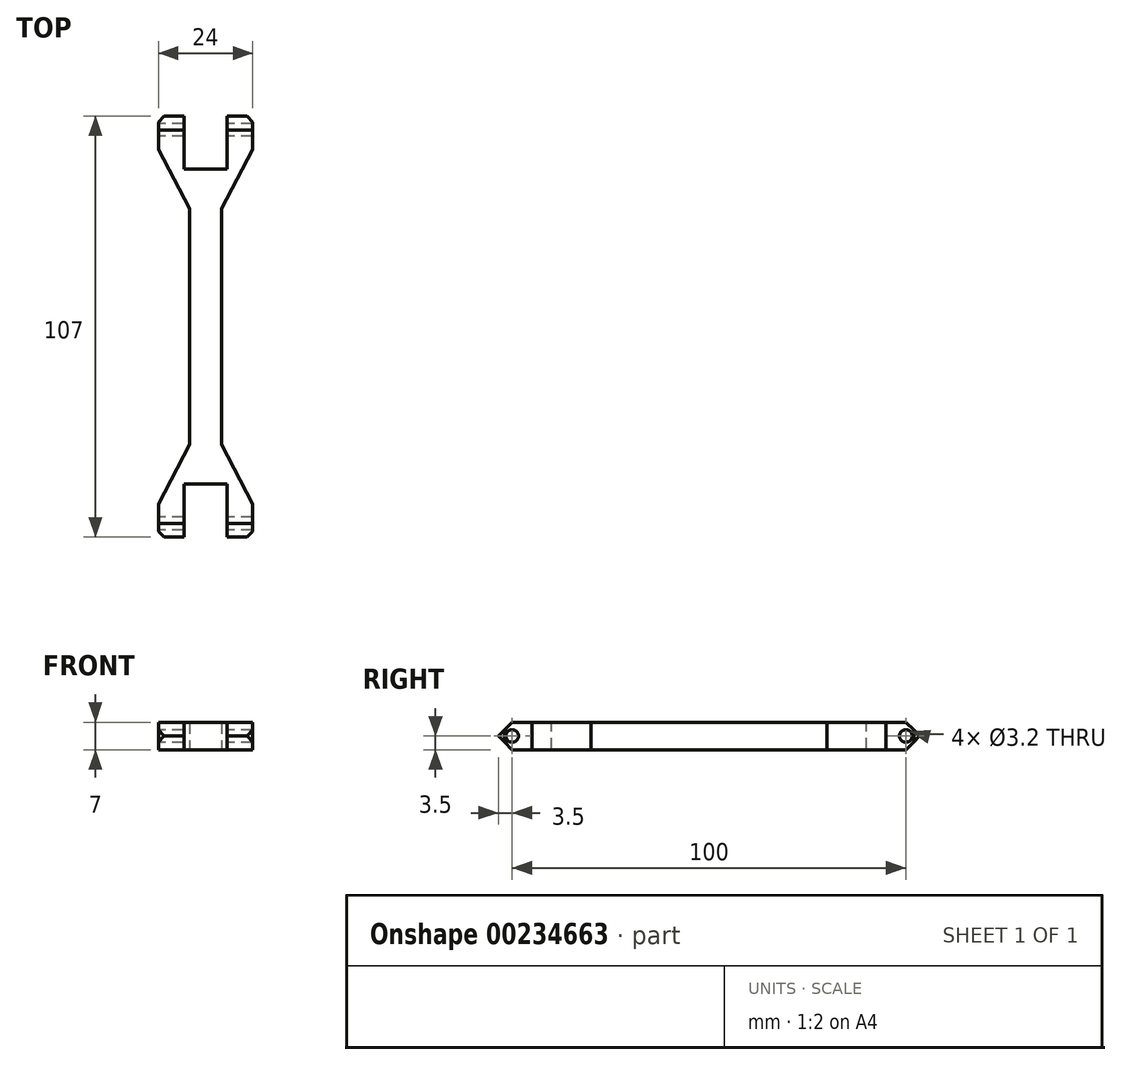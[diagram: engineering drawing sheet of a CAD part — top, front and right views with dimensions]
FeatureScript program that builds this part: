
annotation { "Feature Type Name" : "Feature", "Feature Type Description" : "" }
export const myFeature = defineFeature(function(context is Context, id is Id, definition is map)
    precondition{}
    {
        {
            var Q0;
            Q0=qCreatedBy(makeId("Top.planeOp"),FACE);
            var sketch = newSketch(context, id + "F0", { "sketchPlane" : qUnion([Q0])});
            skLineSegment(sketch, "E0.bottom", {"start": v(-4, 45) * mm, "end": v(4, 45) * mm});
            skLineSegment(sketch, "E0.top", {"start": v(-4, -45) * mm, "end": v(4, -45) * mm});
            skLineSegment(sketch, "E0.left", {"start": v(-4, 45) * mm, "end": v(-4, -45) * mm});
            skLineSegment(sketch, "E0.right", {"start": v(4, 45) * mm, "end": v(4, -45) * mm});
            skPoint(sketch, "E0.middle", {"position": v(0, 0) * mm});
            skLineSegment(sketch, "E1", {"start": v(-4, 45) * mm, "end": v(-12, 45) * mm});
            skLineSegment(sketch, "E2", {"start": v(4, 45) * mm, "end": v(12, 45) * mm});
            skLineSegment(sketch, "E3", {"start": v(12, 45) * mm, "end": v(12, 55) * mm});
            skLineSegment(sketch, "E4", {"start": v(-12, 45) * mm, "end": v(-12, 55) * mm});
            skLineSegment(sketch, "E5", {"start": v(-12, 55) * mm, "end": v(-5.5, 55) * mm});
            skLineSegment(sketch, "E6", {"start": v(12, 55) * mm, "end": v(5.5, 55) * mm});
            skLineSegment(sketch, "E7", {"start": v(-5.5, 55) * mm, "end": v(-5.5, 45) * mm});
            skLineSegment(sketch, "E8", {"start": v(-5.5, 45) * mm, "end": v(5.5, 45) * mm});
            skLineSegment(sketch, "E9", {"start": v(5.5, 45) * mm, "end": v(5.5, 55) * mm});
            skLineSegment(sketch, "E10", {"start": v(4, -45) * mm, "end": v(12, -45) * mm});
            skLineSegment(sketch, "E11", {"start": v(-4, -45) * mm, "end": v(-12, -45) * mm});
            skLineSegment(sketch, "E12", {"start": v(-12, -45) * mm, "end": v(-12, -55) * mm});
            skLineSegment(sketch, "E13", {"start": v(12, -45) * mm, "end": v(12, -55) * mm});
            skLineSegment(sketch, "E14", {"start": v(12, -55) * mm, "end": v(5.5, -55) * mm});
            skLineSegment(sketch, "E15", {"start": v(-12, -55) * mm, "end": v(-5.5, -55) * mm});
            skLineSegment(sketch, "E16", {"start": v(-5.5, -55) * mm, "end": v(-5.5, -45) * mm});
            skLineSegment(sketch, "E17", {"start": v(-5.5, -45) * mm, "end": v(5.5, -45) * mm});
            skLineSegment(sketch, "E18", {"start": v(5.5, -45) * mm, "end": v(5.5, -55) * mm});
            skLineSegment(sketch, "E19", {"start": v(0, -45) * mm, "end": v(0, 0) * mm});
            skLineSegment(sketch, "E20", {"start": v(0, 45) * mm, "end": v(0, 0) * mm});
            skLineSegment(sketch, "E21", {"start": v(-12, 45) * mm, "end": v(0, 22.5) * mm});
            skLineSegment(sketch, "E22", {"start": v(0, 22.5) * mm, "end": v(12, 45) * mm});
            skLineSegment(sketch, "E23", {"start": v(12, -45) * mm, "end": v(0, -22.5) * mm});
            skLineSegment(sketch, "E24", {"start": v(0, -22.5) * mm, "end": v(-12, -45) * mm});
            skSolve(sketch);
        }
        {
            var Q0;
            {var subQ3=sQuery(id+"F0.wireOp",EDGE,"E0.bottom");Q0=makeQuery(id+"F0.imprint","IMPRINT",FACE,{"disambiguationData":[TD([[makeQuery(id+"F0.imprint","IMPRINT",EDGE,{"derivedFrom":subQ3}),-1.0]])]});}
            var Q1;
            {var subQ0=sQuery(id+"F0.wireOp",EDGE,"E1");Q1=makeQuery(id+"F0.imprint","IMPRINT",FACE,{"disambiguationData":[TD([[makeQuery(id+"F0.imprint","IMPRINT",EDGE,{"derivedFrom":subQ0}),1.0]])]});}
            var Q2;
            Q2=makeQuery(id+"F0.imprint","IMPRINT",FACE,{"disambiguationData":[TD([[makeQuery(id+"F0.imprint","IMPRINT",EDGE,{"derivedFrom":sQuery(id+"F0.wireOp",EDGE,"E0.bottom")}),1.0]])]});
            var Q3;
            Q3=makeQuery(id+"F0.imprint","IMPRINT",FACE,{"disambiguationData":[TD([[makeQuery(id+"F0.imprint","IMPRINT",EDGE,{"derivedFrom":sQuery(id+"F0.wireOp",EDGE,"E0.top")}),-1.0]])]});
            var Q4;
            {var subQ0=sQuery(id+"F0.wireOp",EDGE,"E10");Q4=makeQuery(id+"F0.imprint","IMPRINT",FACE,{"disambiguationData":[TD([[makeQuery(id+"F0.imprint","IMPRINT",EDGE,{"derivedFrom":subQ0}),1.0]])]});}
            var Q5;
            {var subQ3=sQuery(id+"F0.wireOp",EDGE,"cfKpiMNQ-YmFG-QDXa-ybqN-YLsFEOFvvFe6");Q5=makeQuery(id+"F0.imprint","IMPRINT",FACE,{"disambiguationData":[TD([[makeQuery(id+"F0.imprint","IMPRINT",EDGE,{"derivedFrom":subQ3}),1.0]])]});}
            var Q6;
            {var subQ0=sQuery(id+"F0.wireOp",EDGE,"E11");Q6=makeQuery(id+"F0.imprint","IMPRINT",FACE,{"disambiguationData":[TD([[makeQuery(id+"F0.imprint","IMPRINT",EDGE,{"derivedFrom":subQ0}),-1.0]])]});}
            var Q7;
            {var subQ0=sQuery(id+"F0.wireOp",EDGE,"E2");Q7=makeQuery(id+"F0.imprint","IMPRINT",FACE,{"disambiguationData":[TD([[makeQuery(id+"F0.imprint","IMPRINT",EDGE,{"derivedFrom":subQ0}),-1.0]])]});}
            var Q8;
            {var subQ3=sQuery(id+"F0.wireOp",EDGE,"P5ZGW9Wr-uCcD-RAwQ-2Qk7-HA82AO7tK8vU");Q8=makeQuery(id+"F0.imprint","IMPRINT",FACE,{"disambiguationData":[TD([[makeQuery(id+"F0.imprint","IMPRINT",EDGE,{"derivedFrom":subQ3}),-1.0]])]});}
            var Q9;
            {var subQ0=sQuery(id+"F0.wireOp",EDGE,"E21");var subQ3=sQuery(id+"F0.wireOp",EDGE,"E0.left");var subQ4=makeQuery(id+"F0.imprint","INTERSECT",VERTEX,{"derivedFrom":[subQ3,subQ0]});Q9=makeQuery(id+"F0.imprint","IMPRINT",FACE,{"disambiguationData":[TD([[makeQuery(id+"F0.imprint","IMPRINT",EDGE,{"disambiguationData":[TD([[subQ4,-1.0]])],"derivedFrom":subQ3}),1.0]])]});}
            var Q10;
            {var subQ1=sQuery(id+"F0.wireOp",EDGE,"E0.top");var subQ3=sQuery(id+"F0.wireOp",EDGE,"E19");var subQ4=makeQuery(id+"F0.imprint","INTERSECT",VERTEX,{"derivedFrom":[subQ1,subQ3]});Q10=makeQuery(id+"F0.imprint","IMPRINT",FACE,{"disambiguationData":[TD([[makeQuery(id+"F0.imprint","IMPRINT",EDGE,{"disambiguationData":[TD([[subQ4,-1.0]])],"derivedFrom":subQ1}),1.0]])]});}
            var Q11;
            {var subQ1=sQuery(id+"F0.wireOp",EDGE,"E0.top");var subQ3=sQuery(id+"F0.wireOp",EDGE,"E19");var subQ4=makeQuery(id+"F0.imprint","INTERSECT",VERTEX,{"derivedFrom":[subQ1,subQ3]});Q11=makeQuery(id+"F0.imprint","IMPRINT",FACE,{"disambiguationData":[TD([[makeQuery(id+"F0.imprint","IMPRINT",EDGE,{"disambiguationData":[TD([[subQ4,1.0]])],"derivedFrom":subQ1}),1.0]])]});}
            var Q12;
            {var subQ0=sQuery(id+"F0.wireOp",EDGE,"E22");var subQ3=sQuery(id+"F0.wireOp",EDGE,"E0.right");var subQ4=makeQuery(id+"F0.imprint","INTERSECT",VERTEX,{"derivedFrom":[subQ3,subQ0]});Q12=makeQuery(id+"F0.imprint","IMPRINT",FACE,{"disambiguationData":[TD([[makeQuery(id+"F0.imprint","IMPRINT",EDGE,{"disambiguationData":[TD([[subQ4,-1.0]])],"derivedFrom":subQ3}),-1.0]])]});}
            var Q13;
            {var subQ0=sQuery(id+"F0.wireOp",EDGE,"E8");var subQ1=sQuery(id+"F0.wireOp",EDGE,"E0.left");var subQ2=makeQuery(id+"F0.imprint","INTERSECT",VERTEX,{"derivedFrom":[subQ1,subQ0]});Q13=makeQuery(id+"F0.imprint","IMPRINT",FACE,{"disambiguationData":[TD([[makeQuery(id+"F0.imprint","IMPRINT",EDGE,{"disambiguationData":[TD([[subQ2,-1.0]])],"derivedFrom":subQ1}),1.0]])]});}
            var Q14;
            {var subQ0=sQuery(id+"F0.wireOp",EDGE,"E8");var subQ1=sQuery(id+"F0.wireOp",EDGE,"E0.right");var subQ2=makeQuery(id+"F0.imprint","INTERSECT",VERTEX,{"derivedFrom":[subQ1,subQ0]});Q14=makeQuery(id+"F0.imprint","IMPRINT",FACE,{"disambiguationData":[TD([[makeQuery(id+"F0.imprint","IMPRINT",EDGE,{"disambiguationData":[TD([[subQ2,-1.0]])],"derivedFrom":subQ1}),-1.0]])]});}
            var Q15;
            Q15=makeQuery(id+"F0.imprint","IMPRINT",FACE,{"disambiguationData":[TD([[makeQuery(id+"F0.imprint","IMPRINT",EDGE,{"derivedFrom":sQuery(id+"F0.wireOp",EDGE,"E2")}),1.0]])]});
            var Q16;
            Q16=makeQuery(id+"F0.imprint","IMPRINT",FACE,{"disambiguationData":[TD([[makeQuery(id+"F0.imprint","IMPRINT",EDGE,{"derivedFrom":sQuery(id+"F0.wireOp",EDGE,"E1")}),-1.0]])]});
            var Q17;
            Q17=makeQuery(id+"F0.imprint","IMPRINT",FACE,{"disambiguationData":[TD([[makeQuery(id+"F0.imprint","IMPRINT",EDGE,{"derivedFrom":sQuery(id+"F0.wireOp",EDGE,"E10")}),-1.0]])]});
            var Q18;
            Q18=makeQuery(id+"F0.imprint","IMPRINT",FACE,{"disambiguationData":[TD([[makeQuery(id+"F0.imprint","IMPRINT",EDGE,{"derivedFrom":sQuery(id+"F0.wireOp",EDGE,"E11")}),1.0]])]});
            var Q19;
            {var subQ0=sQuery(id+"F0.wireOp",EDGE,"E17");var subQ1=sQuery(id+"F0.wireOp",EDGE,"E0.left");var subQ2=makeQuery(id+"F0.imprint","INTERSECT",VERTEX,{"derivedFrom":[subQ1,subQ0]});Q19=makeQuery(id+"F0.imprint","IMPRINT",FACE,{"disambiguationData":[TD([[makeQuery(id+"F0.imprint","IMPRINT",EDGE,{"disambiguationData":[TD([[subQ2,1.0]])],"derivedFrom":subQ1}),1.0]])]});}
            var Q20;
            {var subQ0=sQuery(id+"F0.wireOp",EDGE,"E17");var subQ1=sQuery(id+"F0.wireOp",EDGE,"E0.right");var subQ2=makeQuery(id+"F0.imprint","INTERSECT",VERTEX,{"derivedFrom":[subQ1,subQ0]});Q20=makeQuery(id+"F0.imprint","IMPRINT",FACE,{"disambiguationData":[TD([[makeQuery(id+"F0.imprint","IMPRINT",EDGE,{"disambiguationData":[TD([[subQ2,1.0]])],"derivedFrom":subQ1}),-1.0]])]});}
            extrude(context, id + "F1", {"entities" : qUnion([Q0, Q1, Q2, Q3, Q4, Q5, Q6, Q7, Q8, Q9, Q10, Q11, Q12, Q13, Q14, Q15, Q16, Q17, Q18, Q19, Q20]), "depth" : 7 * mm});
        }
        {
            var Q0;
            Q0=makeQuery(id+"F1.opExtrude","SWEPT_FACE",FACE,{"disambiguationData":[OSD([sQuery(id+"F0.wireOp",EDGE,"E4")])]});
            var sketch = newSketch(context, id + "F2", { "sketchPlane" : qUnion([Q0])});
            skLineSegment(sketch, "E25", {"start": v(-55, 3.5) * mm, "end": v(-50, 3.5) * mm});
            skPoint(sketch, "E25.endSnap0", {"position": v(-50, 7) * mm});
            skLineSegment(sketch, "E26", {"start": v(-50, 3.5) * mm, "end": v(50, 3.5) * mm});
            skCircle(sketch, "E27", {"center": v(-50, 3.5) * mm, "radius": 1.6 * mm});
            skCircle(sketch, "E28", {"center": v(50, 3.5) * mm, "radius": 1.6 * mm});
            skSolve(sketch);
        }
        {
            var Q0;
            {var subQ0=sQuery(id+"F2.wireOp",EDGE,"E26");var subQ1=sQuery(id+"F2.wireOp",EDGE,"E25");var subQ2=makeQuery(id+"F2.imprint","INTERSECT",VERTEX,{"derivedFrom":[subQ1,subQ0]});Q0=makeQuery(id+"F2.imprint","IMPRINT",FACE,{"disambiguationData":[TD([[makeQuery(id+"F2.imprint","IMPRINT",EDGE,{"disambiguationData":[TD([[subQ2,1.0]])],"derivedFrom":subQ1}),1.0]])]});}
            var Q1;
            {var subQ0=sQuery(id+"F2.wireOp",EDGE,"E26");var subQ1=sQuery(id+"F2.wireOp",EDGE,"E25");var subQ2=makeQuery(id+"F2.imprint","INTERSECT",VERTEX,{"derivedFrom":[subQ1,subQ0]});Q1=makeQuery(id+"F2.imprint","IMPRINT",FACE,{"disambiguationData":[TD([[makeQuery(id+"F2.imprint","IMPRINT",EDGE,{"disambiguationData":[TD([[subQ2,1.0]])],"derivedFrom":subQ1}),-1.0]])]});}
            var Q2;
            Q2=makeQuery(id+"F2.imprint","IMPRINT",FACE,{"disambiguationData":[TD([[makeQuery(id+"F2.imprint","IMPRINT",EDGE,{"derivedFrom":sQuery(id+"F2.wireOp",EDGE,"E28")}),1.0]])]});
            extrude(context, id + "F3", {"entities" : qUnion([Q0, Q1, Q2]), "operationType" : NewBodyOperationType.REMOVE, "oppositeDirection" : true, "depth" : 25 * mm});
        }
        {
            var Q0;
            Q0=makeQuery(id+"F1.opExtrude","CAP_FACE",FACE,{"disambiguationData":[OSD([sQuery(id+"F0.wireOp",EDGE,"E0.left"),sQuery(id+"F0.wireOp",EDGE,"E0.right"),sQuery(id+"F0.wireOp",EDGE,"E3"),sQuery(id+"F0.wireOp",EDGE,"E4"),sQuery(id+"F0.wireOp",EDGE,"E5"),sQuery(id+"F0.wireOp",EDGE,"E6"),sQuery(id+"F0.wireOp",EDGE,"E7"),sQuery(id+"F0.wireOp",EDGE,"E8"),sQuery(id+"F0.wireOp",EDGE,"E9"),sQuery(id+"F0.wireOp",EDGE,"E12"),sQuery(id+"F0.wireOp",EDGE,"E13"),sQuery(id+"F0.wireOp",EDGE,"E14"),sQuery(id+"F0.wireOp",EDGE,"E15"),sQuery(id+"F0.wireOp",EDGE,"E16"),sQuery(id+"F0.wireOp",EDGE,"E17"),sQuery(id+"F0.wireOp",EDGE,"E18"),sQuery(id+"F0.wireOp",EDGE,"E21"),sQuery(id+"F0.wireOp",EDGE,"E22"),sQuery(id+"F0.wireOp",EDGE,"E23"),sQuery(id+"F0.wireOp",EDGE,"E24")])],"isStart":false});
            var sketch = newSketch(context, id + "F4", { "sketchPlane" : qUnion([Q0])});
            skLineSegment(sketch, "E29.bottom", {"start": v(-5.5, 45) * mm, "end": v(5.5, 45) * mm});
            skLineSegment(sketch, "E29.top", {"start": v(-5.5, 40) * mm, "end": v(5.5, 40) * mm});
            skLineSegment(sketch, "E29.left", {"start": v(-5.5, 45) * mm, "end": v(-5.5, 40) * mm});
            skLineSegment(sketch, "E29.right", {"start": v(5.5, 45) * mm, "end": v(5.5, 40) * mm});
            skLineSegment(sketch, "E30.bottom", {"start": v(-5.5, -45) * mm, "end": v(5.5, -45) * mm});
            skLineSegment(sketch, "E30.top", {"start": v(-5.5, -40) * mm, "end": v(5.5, -40) * mm});
            skLineSegment(sketch, "E30.left", {"start": v(-5.5, -45) * mm, "end": v(-5.5, -40) * mm});
            skLineSegment(sketch, "E30.right", {"start": v(5.5, -45) * mm, "end": v(5.5, -40) * mm});
            skSolve(sketch);
        }
        {
            var Q0;
            Q0=makeQuery(id+"F4.imprint","IMPRINT",FACE,{"disambiguationData":[TD([[makeQuery(id+"F4.imprint","IMPRINT",EDGE,{"derivedFrom":sQuery(id+"F4.wireOp",EDGE,"E30.bottom")}),1.0]])]});
            var Q1;
            Q1=makeQuery(id+"F4.imprint","IMPRINT",FACE,{"disambiguationData":[TD([[makeQuery(id+"F4.imprint","IMPRINT",EDGE,{"derivedFrom":sQuery(id+"F4.wireOp",EDGE,"E29.bottom")}),-1.0]])]});
            extrude(context, id + "F5", {"entities" : qUnion([Q0, Q1]), "operationType" : NewBodyOperationType.REMOVE, "oppositeDirection" : true, "depth" : 25 * mm});
        }
        {
            var Q0;
            Q0=makeQuery(id+"F1.opExtrude","SWEPT_EDGE",EDGE,{"disambiguationData":[OSD([sQuery(id+"F0.wireOp",EDGE,"E13"),sQuery(id+"F0.wireOp",EDGE,"E14")])]});
            var Q1;
            Q1=makeQuery(id+"F1.opExtrude","SWEPT_EDGE",EDGE,{"disambiguationData":[OSD([sQuery(id+"F0.wireOp",EDGE,"E12"),sQuery(id+"F0.wireOp",EDGE,"E15")])]});
            var Q2;
            Q2=makeQuery(id+"F1.opExtrude","SWEPT_EDGE",EDGE,{"disambiguationData":[OSD([sQuery(id+"F0.wireOp",EDGE,"E3"),sQuery(id+"F0.wireOp",EDGE,"E6")])]});
            var Q3;
            Q3=makeQuery(id+"F1.opExtrude","SWEPT_EDGE",EDGE,{"disambiguationData":[OSD([sQuery(id+"F0.wireOp",EDGE,"E4"),sQuery(id+"F0.wireOp",EDGE,"E5")])]});
            chamfer(context, id + "F6", {"entities" : qUnion([Q0, Q1, Q2, Q3]), "width" : 3 * mm, "tangentPropagation" : true});
        }
        {
            var Q0;
            Q0=makeQuery(id+"F1.opExtrude","CAP_EDGE",EDGE,{"disambiguationData":[OSD([sQuery(id+"F0.wireOp",EDGE,"E15")])],"isStart":true});
            var Q1;
            Q1=makeQuery(id+"F1.opExtrude","CAP_EDGE",EDGE,{"disambiguationData":[OSD([sQuery(id+"F0.wireOp",EDGE,"E15")])],"isStart":false});
            var Q2;
            Q2=makeQuery(id+"F1.opExtrude","CAP_EDGE",EDGE,{"disambiguationData":[OSD([sQuery(id+"F0.wireOp",EDGE,"E14")])],"isStart":true});
            var Q3;
            Q3=makeQuery(id+"F1.opExtrude","CAP_EDGE",EDGE,{"disambiguationData":[OSD([sQuery(id+"F0.wireOp",EDGE,"E14")])],"isStart":false});
            var Q4;
            Q4=makeQuery(id+"F1.opExtrude","CAP_EDGE",EDGE,{"disambiguationData":[OSD([sQuery(id+"F0.wireOp",EDGE,"E6")])],"isStart":false});
            var Q5;
            Q5=makeQuery(id+"F1.opExtrude","CAP_EDGE",EDGE,{"disambiguationData":[OSD([sQuery(id+"F0.wireOp",EDGE,"E6")])],"isStart":true});
            var Q6;
            Q6=makeQuery(id+"F1.opExtrude","CAP_EDGE",EDGE,{"disambiguationData":[OSD([sQuery(id+"F0.wireOp",EDGE,"E5")])],"isStart":false});
            var Q7;
            Q7=makeQuery(id+"F1.opExtrude","CAP_EDGE",EDGE,{"disambiguationData":[OSD([sQuery(id+"F0.wireOp",EDGE,"E5")])],"isStart":true});
            chamfer(context, id + "F7", {"entities" : qUnion([Q0, Q1, Q2, Q3, Q4, Q5, Q6, Q7]), "width" : 5 * mm, "tangentPropagation" : true});
        }
    });
